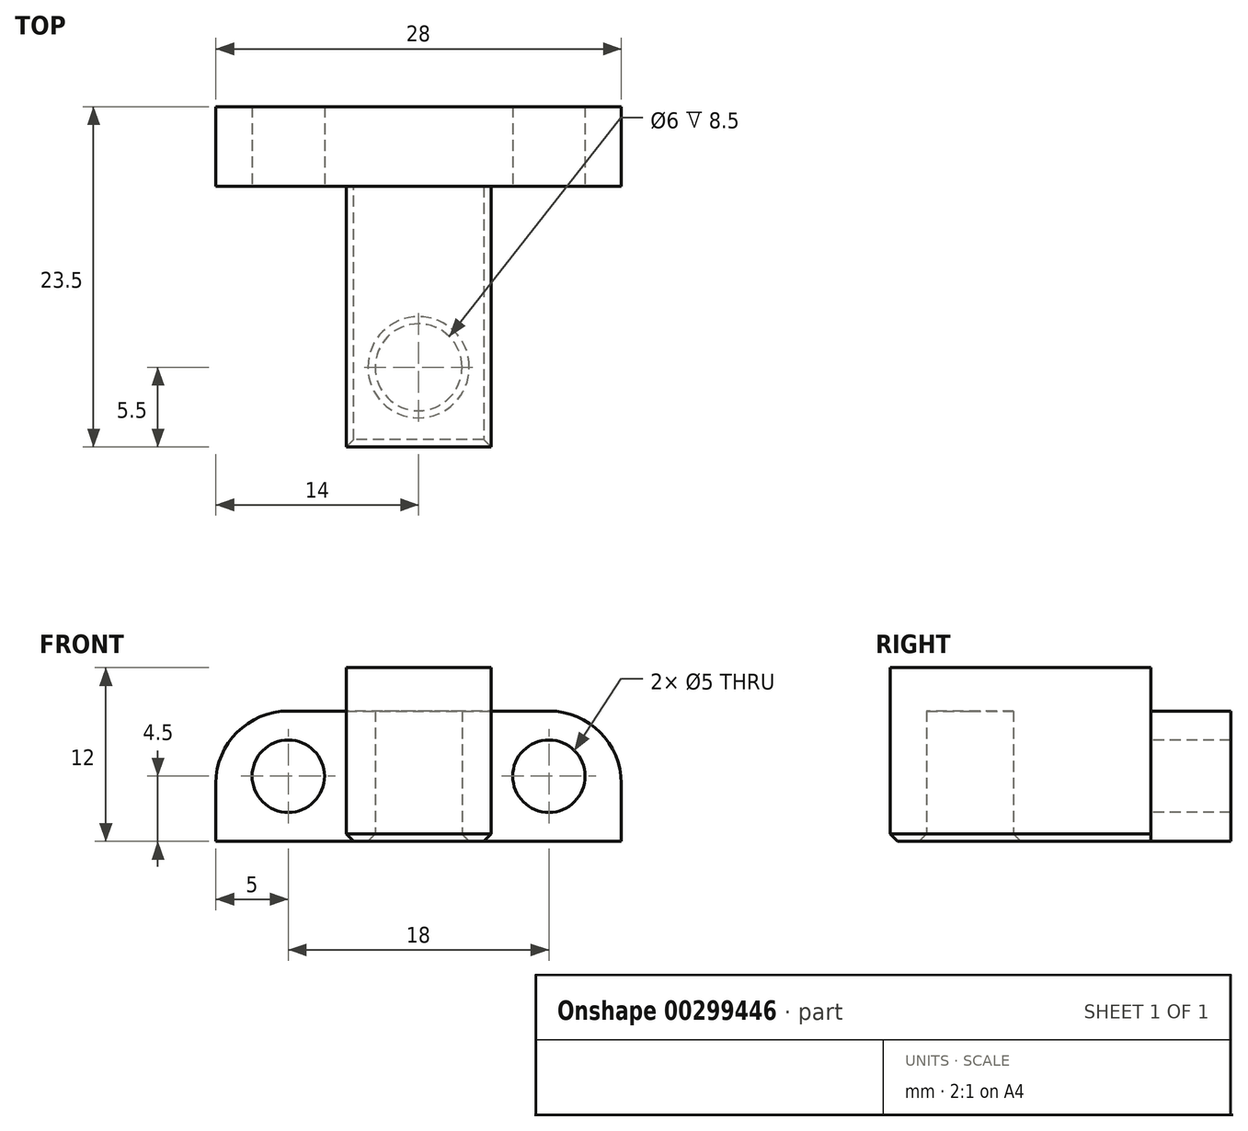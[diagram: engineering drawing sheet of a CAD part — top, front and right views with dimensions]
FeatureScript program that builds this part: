
annotation { "Feature Type Name" : "Feature", "Feature Type Description" : "" }
export const myFeature = defineFeature(function(context is Context, id is Id, definition is map)
    precondition{}
    {
        {
            var Q0;
            Q0=qCreatedBy(makeId("Top.planeOp"),FACE);
            var sketch = newSketch(context, id + "F0", { "sketchPlane" : qUnion([Q0])});
            skCircle(sketch, "E0", {"center": v(0, 0) * mm, "radius": 3 * mm});
            skLineSegment(sketch, "E1.top", {"start": v(5, -5.5) * mm, "end": v(-5, -5.5) * mm});
            skLineSegment(sketch, "E1.left", {"start": v(14, 5.5) * mm, "end": v(14, 0) * mm});
            skLineSegment(sketch, "E1.right", {"start": v(-14, 5.5) * mm, "end": v(-14, 0) * mm});
            skLineSegment(sketch, "E2.top", {"start": v(14, 18) * mm, "end": v(-14, 18) * mm});
            skLineSegment(sketch, "E2.left", {"start": v(14, 5.5) * mm, "end": v(14, 18) * mm});
            skLineSegment(sketch, "E2.right", {"start": v(-14, 10.5) * mm, "end": v(-14, 18) * mm});
            skLineSegment(sketch, "E3", {"start": v(14, 0) * mm, "end": v(-14, 0) * mm, "construction": true});
            skLineSegment(sketch, "E4", {"start": v(0, -5.5) * mm, "end": v(0, 18) * mm, "construction": true});
            skLineSegment(sketch, "E5.top", {"start": v(14, 12.5) * mm, "end": v(5, 12.5) * mm});
            skLineSegment(sketch, "E5.right", {"start": v(5, -5.5) * mm, "end": v(5, 12.5) * mm});
            skLineSegment(sketch, "E6.MirrorCS", {"start": v(-5, -5.5) * mm, "end": v(-5, 12.5) * mm});
            skLineSegment(sketch, "E7.MirrorCS", {"start": v(-14, 12.5) * mm, "end": v(-5, 12.5) * mm});
            skPoint(sketch, "E8.orphan", {"position": v(-14, -5.5) * mm});
            skPoint(sketch, "E9.orphan", {"position": v(14, -5.5) * mm});
            skSolve(sketch);
        }
        {
            var Q0;
            Q0 = qSketchRegion(id + "F0", true);
            extrude(context, id + "F1", {"entities" : qUnion([Q0]), "depth" : 9 * mm, "offsetDistance" : 25 * mm});
        }
        {
            var Q0;
            Q0=makeQuery(id+"F1.opExtrude","SWEPT_FACE",FACE,{"disambiguationData":[OSD([sQuery(id+"F0.wireOp",EDGE,"E7.MirrorCS")])]});
            var sketch = newSketch(context, id + "F2", { "sketchPlane" : qUnion([Q0])});
            skPoint(sketch, "E10", {"position": v(9, 4.5) * mm});
            skLineSegment(sketch, "E11", {"start": v(5, 4.5) * mm, "end": v(5, 4.5) * mm});
            skLineSegment(sketch, "E12", {"start": v(0, 0) * mm, "end": v(0, 9) * mm, "construction": true});
            skPoint(sketch, "E13.MirrorP", {"position": v(-9, 4.5) * mm});
            skSolve(sketch);
        }
        {
            var Q0;
            Q0=sQuery(id+"F2.wireOp",VERTEX,"E10");
            var Q1;
            Q1=sQuery(id+"F2.wireOp",VERTEX,"E13.MirrorP");
            var Q2;
            Q2=makeQuery(id+"F1.opExtrude","SWEPT_BODY",BODY,{"disambiguationData":[OSD([sQuery(id+"F0.wireOp",EDGE,"E0"),sQuery(id+"F0.wireOp",EDGE,"E1.top"),sQuery(id+"F0.wireOp",EDGE,"E1.left"),sQuery(id+"F0.wireOp",EDGE,"E1.right"),sQuery(id+"F0.wireOp",EDGE,"E2.top"),sQuery(id+"F0.wireOp",EDGE,"E2.left"),sQuery(id+"F0.wireOp",EDGE,"E2.right")])]});
            hole(context, id + "F3", {"style" : HoleStyle.SIMPLE, "endStyle" : HoleEndStyle.THROUGH, "standardTappedOrClearance" : lookupTablePath({ "standard" : "ISO", "size" : "5", "type" : "Drilled" }), "standardBlindInLast" : lookupTablePath({ "standard" : "ISO", "size" : "5", "type" : "Drilled" }), "holeDiameter" : 5 * mm, "majorDiameter" : 5 * mm, "isTappedThrough" : true, "tappedDepth" : 9.6 * mm, "tapClearance" : 3, "locations" : qUnion([Q0, Q1]), "scope" : qUnion([Q2])});
        }
        {
            var Q0;
            Q0=makeQuery(id+"F1.opExtrude","CAP_FACE",FACE,{"disambiguationData":[OSD([sQuery(id+"F0.wireOp",EDGE,"E0"),sQuery(id+"F0.wireOp",EDGE,"E1.top"),sQuery(id+"F0.wireOp",EDGE,"E2.top"),sQuery(id+"F0.wireOp",EDGE,"E2.left"),sQuery(id+"F0.wireOp",EDGE,"E2.right"),sQuery(id+"F0.wireOp",EDGE,"E5.top"),sQuery(id+"F0.wireOp",EDGE,"E5.right"),sQuery(id+"F0.wireOp",EDGE,"E6.MirrorCS"),sQuery(id+"F0.wireOp",EDGE,"E7.MirrorCS")])],"isStart":false});
            var sketch = newSketch(context, id + "F4", { "sketchPlane" : qUnion([Q0])});
            skLineSegment(sketch, "E14.bottom", {"start": v(5, -5.5) * mm, "end": v(-5, -5.5) * mm});
            skLineSegment(sketch, "E14.left", {"start": v(5, -5.5) * mm, "end": v(5, 12.5) * mm});
            skLineSegment(sketch, "E14.right", {"start": v(-5, -5.5) * mm, "end": v(-5, 12.5) * mm});
            skLineSegment(sketch, "E15", {"start": v(-5, 12.5) * mm, "end": v(5, 12.5) * mm});
            skPoint(sketch, "E14.top.end.orphan", {"position": v(-5, 18) * mm});
            skSolve(sketch);
        }
        {
            var Q0;
            Q0 = qSketchRegion(id + "F4", true);
            extrude(context, id + "F5", {"entities" : qUnion([Q0]), "operationType" : NewBodyOperationType.ADD, "depth" : 3 * mm, "offsetDistance" : 25 * mm});
        }
        {
            var Q0;
            Q0=makeQuery(id+"F1.opExtrude","CAP_EDGE",EDGE,{"disambiguationData":[OSD([sQuery(id+"F0.wireOp",EDGE,"E2.left")])],"isStart":false});
            var Q1;
            Q1=makeQuery(id+"F1.opExtrude","CAP_EDGE",EDGE,{"disambiguationData":[OSD([sQuery(id+"F0.wireOp",EDGE,"E2.right")])],"isStart":false});
            fillet(context, id + "F6", {"entities" : qUnion([Q0, Q1]), "radius" : 5 * mm, "tangentPropagation" : true, "allowEdgeOverflow" : false});
        }
        {
            var Q0;
            Q0=makeQuery(id+"F3.hole-1.boolean.opBoolean","COPY",EDGE,{"derivedFrom":makeQuery(id+"F3.hole-1.opRevolve","SWEPT_EDGE",EDGE,{"disambiguationData":[OSD([sQuery(id+"F3.hole-1.sketch.wireOp",EDGE,"core_line_2"),sQuery(id+"F3.hole-1.sketch.wireOp",EDGE,"core_line_3")])]})});
            var Q1;
            Q1=makeQuery(id+"F3.hole-0.boolean.opBoolean","COPY",EDGE,{"derivedFrom":makeQuery(id+"F3.hole-0.opRevolve","SWEPT_EDGE",EDGE,{"disambiguationData":[OSD([sQuery(id+"F3.hole-0.sketch.wireOp",EDGE,"core_line_2"),sQuery(id+"F3.hole-0.sketch.wireOp",EDGE,"core_line_3")])]})});
            var Q2;
            Q2=makeQuery(id+"F1.opExtrude","CAP_EDGE",EDGE,{"disambiguationData":[OSD([sQuery(id+"F0.wireOp",EDGE,"E0")])],"isStart":true});
            var Q3;
            Q3=makeQuery(id+"F1.opExtrude","CAP_EDGE",EDGE,{"disambiguationData":[OSD([sQuery(id+"F0.wireOp",EDGE,"E5.right")])],"isStart":true});
            var Q4;
            Q4=makeQuery(id+"F1.opExtrude","CAP_EDGE",EDGE,{"disambiguationData":[OSD([sQuery(id+"F0.wireOp",EDGE,"E6.MirrorCS")])],"isStart":true});
            var Q5;
            Q5=makeQuery(id+"F1.opExtrude","CAP_EDGE",EDGE,{"disambiguationData":[OSD([sQuery(id+"F0.wireOp",EDGE,"E1.top")])],"isStart":true});
            chamfer(context, id + "F7", {"entities" : qUnion([Q0, Q1, Q2, Q3, Q4, Q5]), "width" : 0.5 * mm, "tangentPropagation" : true});
        }
    });
